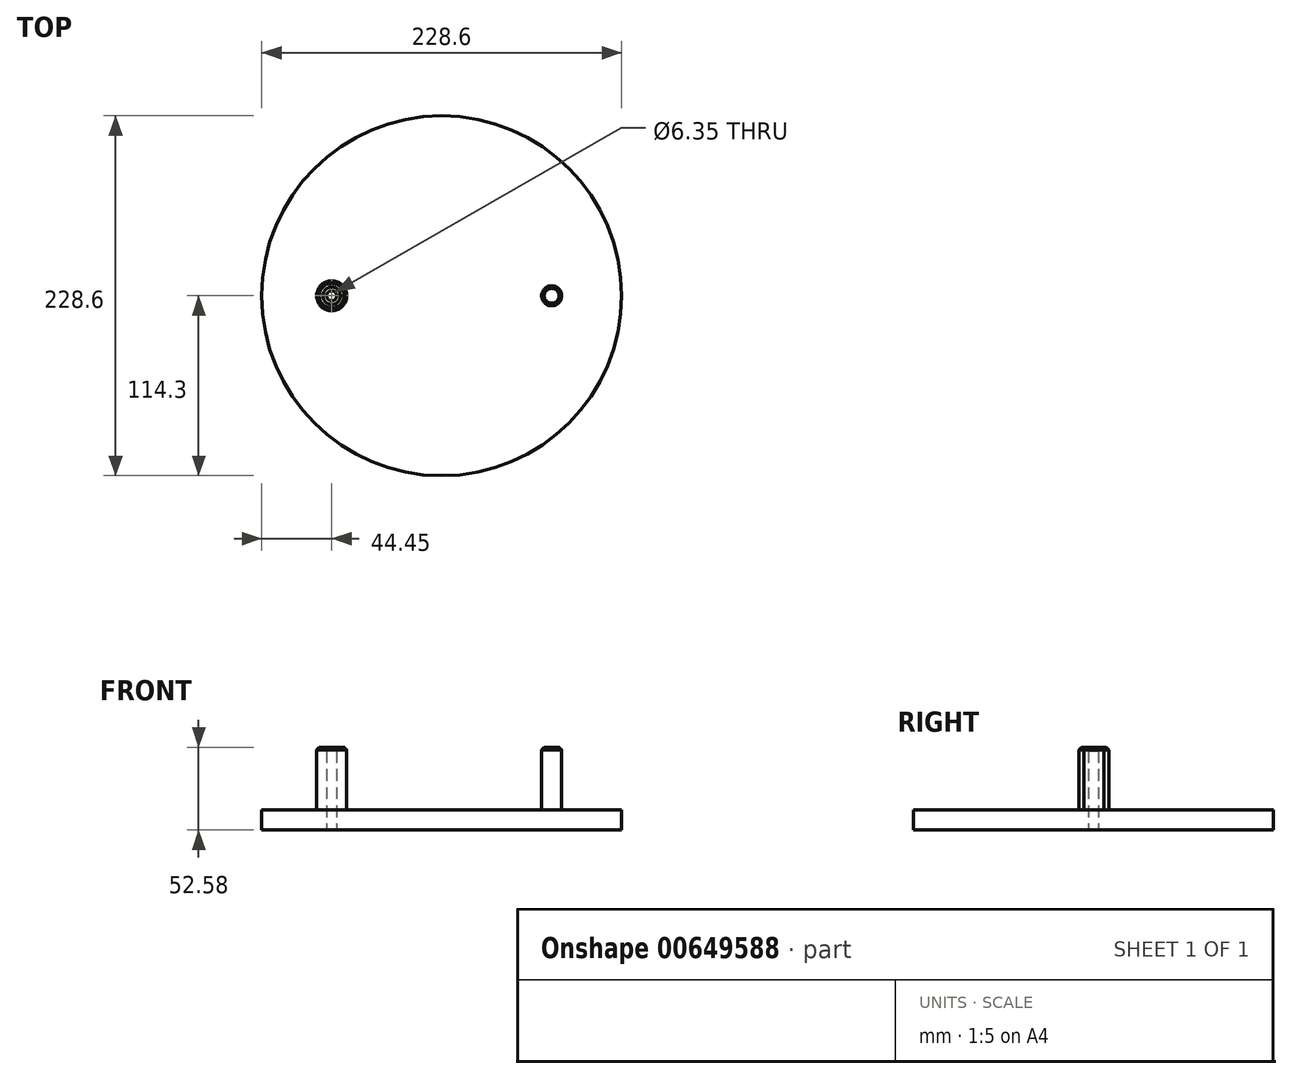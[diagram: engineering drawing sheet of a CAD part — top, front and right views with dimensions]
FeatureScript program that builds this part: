
annotation { "Feature Type Name" : "Feature", "Feature Type Description" : "" }
export const myFeature = defineFeature(function(context is Context, id is Id, definition is map)
    precondition{}
    {
        {
            var Q0;
            Q0=qCreatedBy(makeId("Top.planeOp"),FACE);
            var sketch = newSketch(context, id + "F0", { "sketchPlane" : qUnion([Q0])});
            skCircle(sketch, "E0", {"center": v(0, 0) * mm, "radius": 114.3 * mm});
            skLineSegment(sketch, "E1", {"start": v(-69.85, 0) * mm, "end": v(69.85, 0) * mm, "construction": true});
            skCircle(sketch, "E2", {"center": v(-69.85, 0) * mm, "radius": 3.18 * mm});
            skSolve(sketch);
        }
        {
            var Q0;
            Q0=makeQuery(id+"F0.imprint","IMPRINT",FACE,{"disambiguationData":[TD([[makeQuery(id+"F0.imprint","IMPRINT",EDGE,{"derivedFrom":sQuery(id+"F0.wireOp",EDGE,"E0")}),1.0]])]});
            extrude(context, id + "F1", {"entities" : qUnion([Q0]), "depth" : 12.7 * mm, "offsetDistance" : 25.4 * mm});
        }
        {
            var Q0;
            Q0=makeQuery(id+"F1.opExtrude","CAP_FACE",FACE,{"disambiguationData":[OSD([sQuery(id+"F0.wireOp",EDGE,"E0"),sQuery(id+"F0.wireOp",EDGE,"E2")])],"isStart":false});
            var sketch = newSketch(context, id + "F2", { "sketchPlane" : qUnion([Q0])});
            skLineSegment(sketch, "E3", {"start": v(69.85, 0) * mm, "end": v(-69.85, 0) * mm});
            skCircle(sketch, "E4", {"center": v(-69.85, 0) * mm, "radius": 9.53 * mm});
            skCircle(sketch, "E5", {"center": v(69.85, 0) * mm, "radius": 6.35 * mm});
            skCircle(sketch, "E6", {"center": v(-69.85, 0) * mm, "radius": 3.18 * mm});
            skSolve(sketch);
        }
        {
            var Q0;
            Q0 = qSketchRegion(id + "F2", true);
            extrude(context, id + "F3", {"entities" : qUnion([Q0]), "operationType" : NewBodyOperationType.ADD, "depth" : 39.88 * mm, "offsetDistance" : 25.4 * mm});
        }
        {
            var Q0;
            Q0=makeQuery(id+"F3.opExtrude","CAP_EDGE",EDGE,{"disambiguationData":[OSD([sQuery(id+"F2.wireOp",EDGE,"E6")])],"isStart":false});
            chamfer(context, id + "F4", {"entities" : qUnion([Q0]), "width" : 2.38 * mm, "tangentPropagation" : true});
        }
        {
            var Q0;
            Q0=makeQuery(id+"F3.opExtrude","CAP_EDGE",EDGE,{"disambiguationData":[OSD([sQuery(id+"F2.wireOp",EDGE,"E5")])],"isStart":false});
            chamfer(context, id + "F5", {"entities" : qUnion([Q0]), "width" : 1.59 * mm, "tangentPropagation" : true});
        }
        {
            var Q0;
            Q0=makeQuery(id+"F3.opExtrude","CAP_EDGE",EDGE,{"disambiguationData":[OSD([sQuery(id+"F2.wireOp",EDGE,"E4")])],"isStart":false});
            chamfer(context, id + "F6", {"entities" : qUnion([Q0]), "width" : 1.59 * mm, "tangentPropagation" : true});
        }
    });
